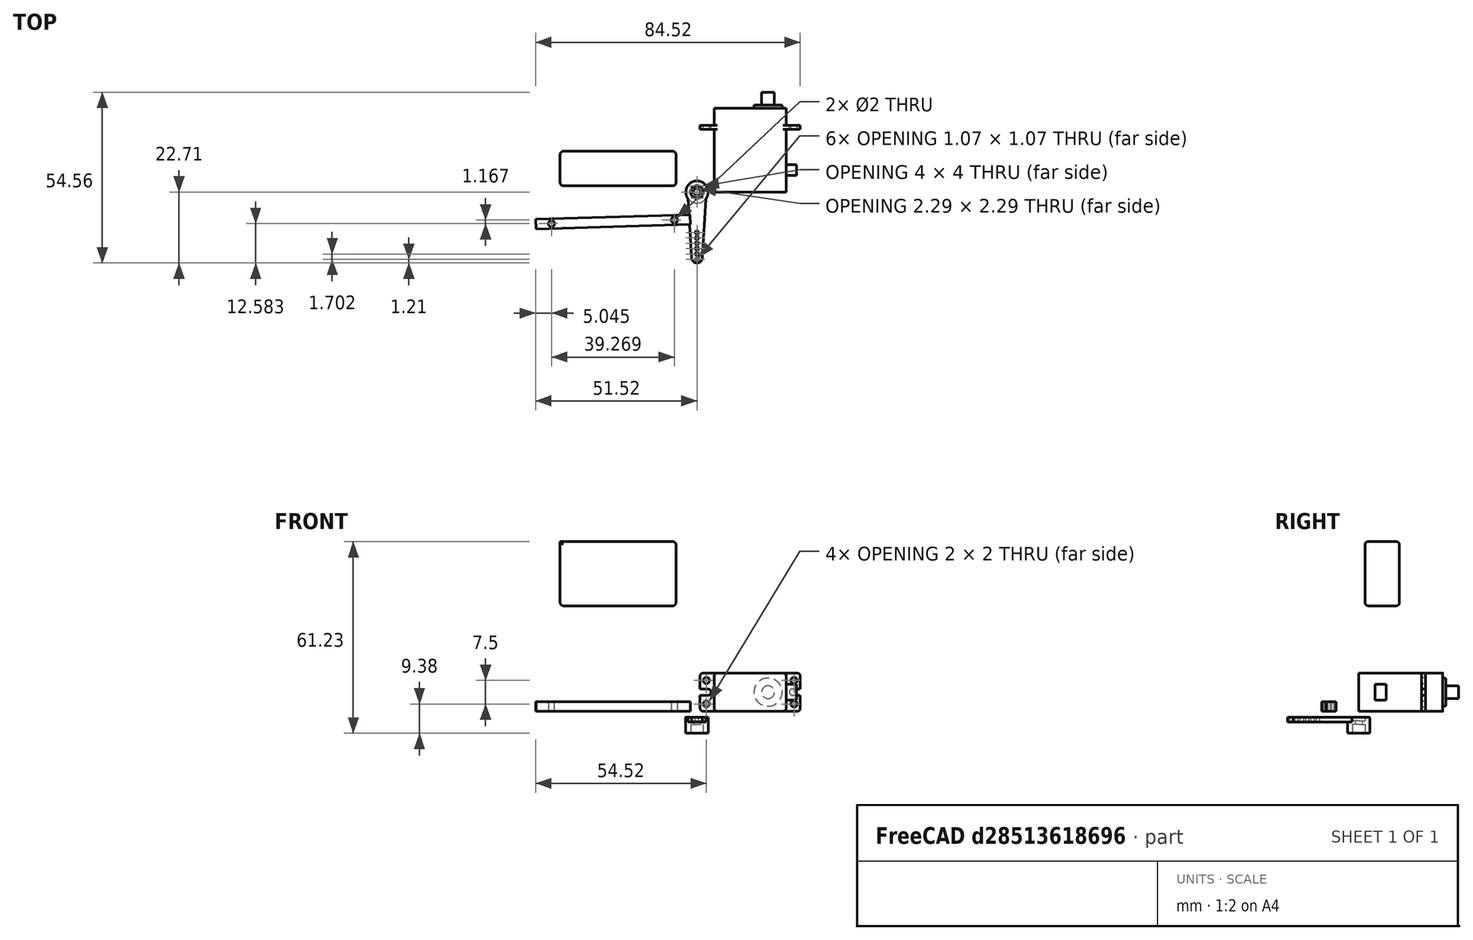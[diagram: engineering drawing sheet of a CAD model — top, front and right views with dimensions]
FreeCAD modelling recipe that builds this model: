
FCSTD DOCUMENT  (FreeCAD 0.20R29603 (Git))
Label: ServoMount
License: All rights reserved
LicenseURL: http://en.wikipedia.org/wiki/All_rights_reserved
objects: PartDesign::CoordinateSystem×6, Part::Feature×3, App::DocumentObjectGroup×3, App::Link×3, App::Part×3, PartDesign::Line×2, App::FeaturePython×1, Sketcher::SketchObject×1, PartDesign::Pad×1, PartDesign::Body×1
note: 15 computed .brp shape members not serialized (recipe doc carries the construction recipe); baked Part::Feature solids carry a one-line shape summary decoded from their .brp

FEATURE [Part::Feature] Part__Feature005  label="servo_model"
  shape: bbox 32 x 31.85 x 12.2 mm, 70 faces (baked)
FEATURE [Part::Feature] Part__Feature006  label="Turnigy 180mah 2s"
  Placement = pos=(-30.6953,2,43.9546) rot=(0,1,0;1.5708rad)
  shape: bbox 37 x 11 x 20.5 mm, 23 faces (baked)
FEATURE [Part::Feature] Part__Feature007  label="servo_arm_model"
  shape: bbox 7.137 x 26.28 x 5.16 mm, 28 faces (baked)
FEATURE [PartDesign::CoordinateSystem] LCS_0
  AttacherType = Attacher::AttachEngine3D
  MapMode = 11
  Placement = pos=(-5.5,4e-16,-7.03297) rot=(0,0,1;1.5708rad)
  Support = -> [Part__Feature007]
FEATURE [PartDesign::CoordinateSystem] LCS_1
  AttacherType = Attacher::AttachEngine3D
  Support = -> [Part__Feature005]
FEATURE [PartDesign::CoordinateSystem] LCS_Origin
  AttacherType = Attacher::AttachEngine3D
  MapMode = 2
  Support = -> [X_Axis002]
FEATURE [App::DocumentObjectGroup] Constraints
FEATURE [App::FeaturePython] Variables  # WARN: FeaturePython — macro-defined, semantics opaque (R4)
  Type = App::PropertyContainer
  servoArmRotation = 0
FEATURE [App::DocumentObjectGroup] Configurations
FEATURE [App::Link] servo_part  label="servo_part001"
  AttachedBy = #LCS_1
  AttachedTo = Parent Assembly#LCS_Origin
  LinkedObject = -> Part
  SolverId = Asm4EE
  expr: Placement = LCS_Origin.Placement * AttachmentOffset * LCS_1.Placement ^ -1
FEATURE [App::Link] servo_arm001
  AttachedBy = #LCS_0
  AttachedTo = servo_part#servo_drive
  AttachmentOffset = pos=(0,0,-4) rot=(0,0,1;0rad)
  LinkPlacement = pos=(17.2,34.883,0.6) rot=(-0.57735,0.57735,0.57735;2.0944rad)
  LinkedObject = -> servo_arm
  Placement = pos=(17.2,34.883,0.6) rot=(-0.57735,0.57735,0.57735;2.0944rad)
  SolverId = Asm4EE
  expr: Placement = servo_part.Placement * servo_drive.Placement * AttachmentOffset * LCS_0.Placement ^ -1
FEATURE [PartDesign::CoordinateSystem] servo_drive  label="servo_output_shaft"
  AttacherType = Attacher::AttachEngine3D
  MapMode = 45
  Placement = pos=(17.2,31.85,6.1) rot=(0,0.707107,0.707107;3.14159rad)
  Support = -> [Part__Feature005]
  expr: .AttachmentOffset.Rotation.Angle = Variables.servoArmRotation
FEATURE [App::Part] Part  label="servo_part"
  Group = -> [Part__Feature005,LCS_1,servo_drive]
  Origin = -> Origin
FEATURE [Sketcher::SketchObject] Sketch
  FullyConstrained = false
  MapMode = 5
  Support = -> [XY_Plane003]
  sketch-geometry (8):
    g0: LineSegment StartX=-56.9257 StartY=-11.8541 StartZ=0 EndX=-57.0196 EndY=-8.6971 EndZ=0
    g1: LineSegment StartX=-57.0196 StartY=-8.6971 StartZ=0 EndX=-7.75492 EndY=-7.23288 EndZ=0
    g2: LineSegment StartX=-7.75492 StartY=-7.23288 StartZ=0 EndX=-7.66109 EndY=-10.3899 EndZ=0
    g3: LineSegment StartX=-7.66109 StartY=-10.3899 StartZ=0 EndX=-56.9257 EndY=-11.8541 EndZ=0
    g4: Circle CenterX=-51.9748 CenterY=-10.1271 CenterZ=0 NormalX=0 NormalY=0 NormalZ=1 AngleXU=0 Radius=1
    g5: Circle CenterX=-12.7058 CenterY=-8.95993 CenterZ=0 NormalX=0 NormalY=0 NormalZ=1 AngleXU=0 Radius=1
    g6: LineSegment StartX=-51.9279 StartY=-11.7056 StartZ=0 EndX=-52.0218 EndY=-8.54856 EndZ=0
    g7: LineSegment StartX=-12.6589 StartY=-10.5384 StartZ=0 EndX=-12.7527 EndY=-7.38142 EndZ=0
  constraints (19):
    c: Coincident(g0,g1)
    c: Coincident(g1,g2)
    c: Coincident(g2,g3)
    c: Coincident(g3,g0)
    c: Perpendicular(g2,g3)
    c: Perpendicular(g1,g2)
    c: Perpendicular(g0,g3)
    c: PointOnObject(g6,g3)
    c: PointOnObject(g6,g1)
    c: Symmetric(g6,g6,g4)
    c: Perpendicular(g3,g6)
    c: Distance(g4,g0) = 5
    c: PointOnObject(g7,g3)
    c: PointOnObject(g7,g1)
    c: Perpendicular(g3,g7)
    c: Distance(g7,g2) = 5
    c: Symmetric(g7,g7,g5)
    c: Equal(g5,g4)
    c: Diameter(g5) = 2
FEATURE [PartDesign::Pad] Pad
  Direction = (0,0,1)
  Length = 3
  Length2 = 10
  Profile = -> Sketch
  ReferenceAxis = -> Sketch [N_Axis]
  Type = 0
FEATURE [PartDesign::CoordinateSystem] LCS_2
  AttacherType = Attacher::AttachEngine3D
  Support = -> [Pad]
FEATURE [PartDesign::Line] HoleAxis_1
  AttacherType = Attacher::AttachEngineLine
  Length = 6.29438
  MapMode = 19
  Placement = pos=(-12.7058,-8.95993,0) rot=(0,0,1;0rad)
  ResizeMode = 1
  Support = -> [Pad]
FEATURE [PartDesign::Line] HoleAxis_2
  AttacherType = Attacher::AttachEngineLine
  Length = 6.6495
  MapMode = 19
  Placement = pos=(-51.9748,-10.1271,0) rot=(0,0,1;0rad)
  ResizeMode = 1
  Support = -> [Pad]
FEATURE [PartDesign::Body] Body  label="arm"
  Group = -> [Sketch,Pad,LCS_2,HoleAxis_1,HoleAxis_2]
  Origin = -> Origin003
  Tip = -> Pad
FEATURE [PartDesign::CoordinateSystem] LCS_3
  AttacherType = Attacher::AttachEngine3D
  MapMode = 11
  Placement = pos=(-5.5,-21.5,-1.87297) rot=(0.707107,0.707107,0;3.14159rad)
  Support = -> [Part__Feature007]
  expr: .AttachmentOffset.Rotation.Angle = 0
FEATURE [App::Part] servo_arm
  Group = -> [LCS_0,Part__Feature007,LCS_3]
  Origin = -> Origin001
FEATURE [App::DocumentObjectGroup] Parts
  Group = -> [Part,servo_arm,Body]
FEATURE [App::Link] arm  label="arm001"
  AttachedBy = #HoleAxis_2
  AttachedTo = servo_arm001#LCS_3
  LinkPlacement = pos=(90.6748,33.01,16.2271) rot=(-1,0,0;4.71239rad)
  LinkedObject = -> Body
  Placement = pos=(90.6748,33.01,16.2271) rot=(-1,0,0;4.71239rad)
  SolverId = Asm4EE
  expr: Placement = servo_arm001.Placement * LCS_3.Placement * AttachmentOffset * HoleAxis_2.Placement ^ -1
FEATURE [App::Part] Assembly
  AssemblyType = Part::Link
  Group = -> [LCS_Origin,Constraints,Variables,Configurations,servo_part,servo_arm001,arm]
  Origin = -> Origin002
  Type = Assembly
